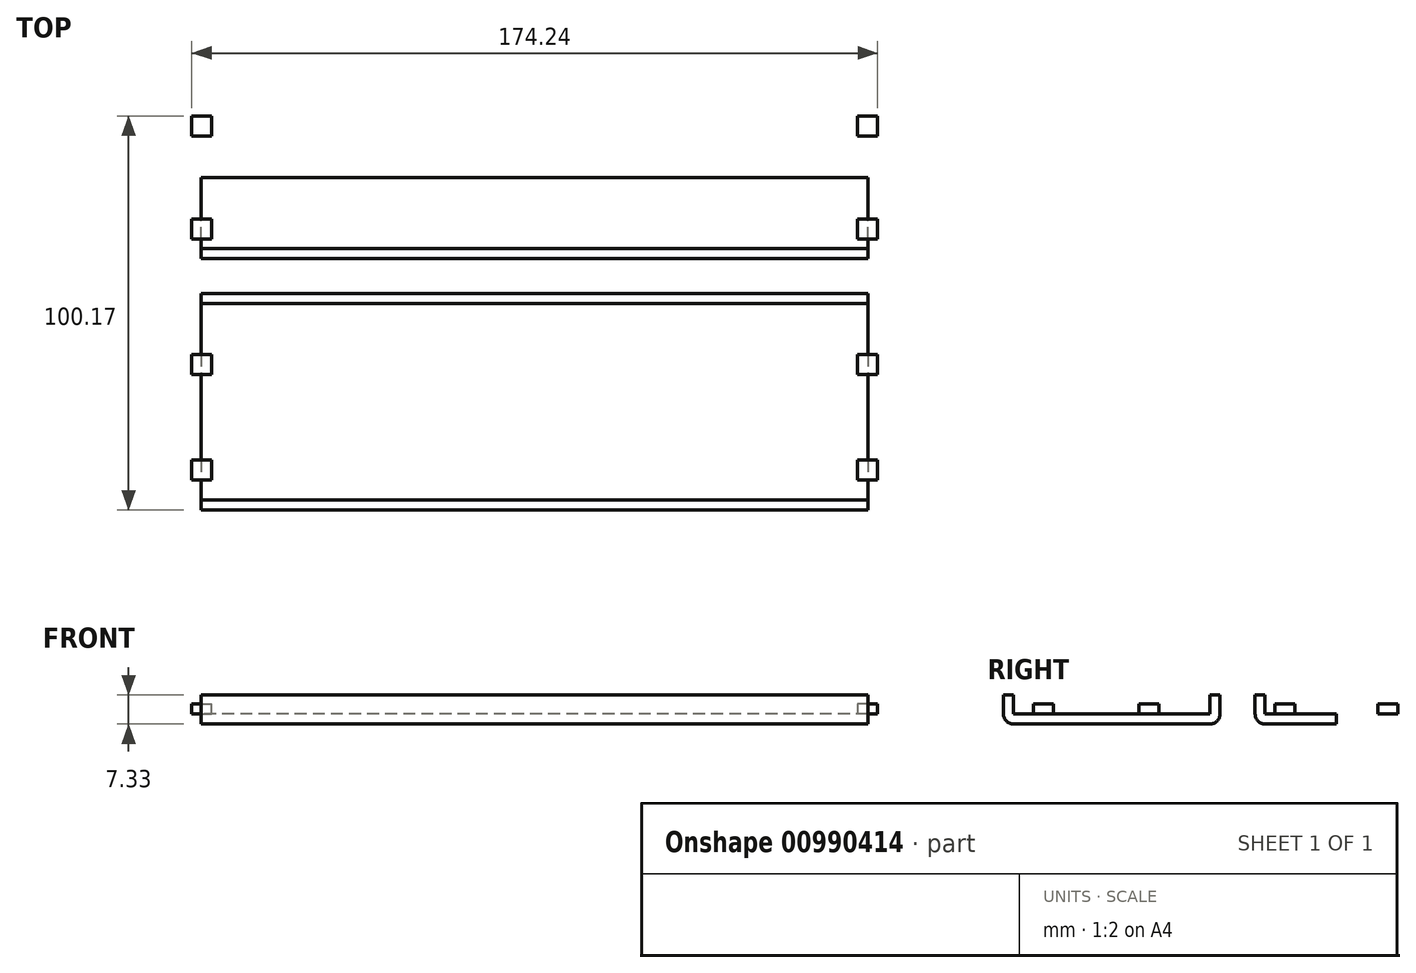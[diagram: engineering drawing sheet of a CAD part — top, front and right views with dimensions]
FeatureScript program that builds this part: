
annotation { "Feature Type Name" : "Feature", "Feature Type Description" : "" }
export const myFeature = defineFeature(function(context is Context, id is Id, definition is map)
    precondition{}
    {
        {
            var Q0;
            Q0=qCreatedBy(makeId("Right.planeOp"),FACE);
            var sketch = newSketch(context, id + "F0", { "sketchPlane" : qUnion([Q0])});
            skLineSegment(sketch, "E0", {"start": v(0, 0) * mm, "end": v(0, 169.34) * mm});
            skLineSegment(sketch, "E1", {"start": v(0, 169.34) * mm, "end": v(200.4, 169.34) * mm});
            skLineSegment(sketch, "E2", {"start": v(0, 0) * mm, "end": v(43.05, 0) * mm, "construction": true});
            skLineSegment(sketch, "E3", {"start": v(43.05, 0) * mm, "end": v(23.47, 45.96) * mm});
            skLineSegment(sketch, "E4", {"start": v(0, 47.82) * mm, "end": v(22.68, 47.82) * mm, "construction": true});
            skLineSegment(sketch, "E5", {"start": v(22.68, 47.82) * mm, "end": v(22.68, 0) * mm, "construction": true});
            skLineSegment(sketch, "E6", {"start": v(23.1, 49.8) * mm, "end": v(40.9, 132) * mm});
            skLineSegment(sketch, "E7", {"start": v(41.4, 134.33) * mm, "end": v(0, 134.33) * mm, "construction": true});
            skLineSegment(sketch, "E8", {"start": v(41.4, 134.33) * mm, "end": v(43.05, 0) * mm, "construction": true});
            skLineSegment(sketch, "E9", {"start": v(43.31, 135.75) * mm, "end": v(72.51, 157.5) * mm});
            skLineSegment(sketch, "E10", {"start": v(74.2, 158.76) * mm, "end": v(74.2, 169.34) * mm, "construction": true});
            skLineSegment(sketch, "E11", {"start": v(74.2, 158.76) * mm, "end": v(0, 158.76) * mm, "construction": true});
            skPoint(sketch, "E12", {"position": v(100.2, 169.34) * mm});
            skLineSegment(sketch, "E13", {"start": v(100.2, 169.34) * mm, "end": v(100.2, 154.3) * mm, "construction": true});
            skLineSegment(sketch, "E14", {"start": v(76.3, 158.76) * mm, "end": v(100.2, 158.76) * mm});
            skLineSegment(sketch, "E15.4", {"start": v(41.18, -0.8) * mm, "end": v(20.56, 47.62) * mm, "construction": true});
            skLineSegment(sketch, "E15.5", {"start": v(20.56, 47.62) * mm, "end": v(39.58, 135.5) * mm});
            skLineSegment(sketch, "E15.6", {"start": v(39.58, 135.5) * mm, "end": v(73.52, 160.79) * mm});
            skLineSegment(sketch, "E15.7", {"start": v(73.52, 160.79) * mm, "end": v(100.2, 160.79) * mm});
            skLineSegment(sketch, "E16.5", {"start": v(11.62, 46.77) * mm, "end": v(31.89, 140.45) * mm});
            skLineSegment(sketch, "E16.6", {"start": v(31.89, 140.45) * mm, "end": v(70.69, 169.35) * mm, "construction": true});
            skLineSegment(sketch, "E16.7", {"start": v(70.69, 169.35) * mm, "end": v(100.2, 169.35) * mm});
            skLineSegment(sketch, "E17", {"start": v(31.89, 140.45) * mm, "end": v(38.14, 169.34) * mm, "construction": true});
            skLineSegment(sketch, "E18", {"start": v(10.6, 158.76) * mm, "end": v(0, 158.76) * mm, "construction": true});
            skLineSegment(sketch, "E19", {"start": v(10.6, 158.76) * mm, "end": v(10.6, 46.77) * mm});
            skLineSegment(sketch, "E20", {"start": v(10.6, 46.77) * mm, "end": v(11.62, 46.77) * mm});
            skLineSegment(sketch, "E21", {"start": v(36.3, 160.79) * mm, "end": v(31.89, 140.45) * mm, "construction": true});
            skLineSegment(sketch, "E22", {"start": v(41.4, 134.33) * mm, "end": v(48.98, 169.34) * mm, "construction": true});
            skLineSegment(sketch, "E23", {"start": v(47.13, 160.79) * mm, "end": v(44.8, 150.07) * mm});
            skLineSegment(sketch, "E24", {"start": v(13.2, 0) * mm, "end": v(0, 0) * mm});
            skLineSegment(sketch, "E25", {"start": v(31.54, 0) * mm, "end": v(43.05, 0) * mm});
            skLineSegment(sketch, "E26", {"start": v(100.2, 158.76) * mm, "end": v(100.2, 169.35) * mm});
            skPoint(sketch, "E27", {"position": v(46.69, 158.76) * mm});
            skPoint(sketch, "E28", {"position": v(56.47, 158.76) * mm});
            skLineSegment(sketch, "E29", {"start": v(46.69, 158.76) * mm, "end": v(56.47, 158.76) * mm});
            skLineSegment(sketch, "E30", {"start": v(44.8, 150.07) * mm, "end": v(46.69, 158.76) * mm});
            skLineSegment(sketch, "E31", {"start": v(10.6, 158.76) * mm, "end": v(35.85, 158.76) * mm});
            skLineSegment(sketch, "E32", {"start": v(35.85, 158.76) * mm, "end": v(31.89, 140.45) * mm});
            skLineSegment(sketch, "E33", {"start": v(44.8, 150.07) * mm, "end": v(56.47, 158.76) * mm});
            skLineSegment(sketch, "E34", {"start": v(30.88, 85.7) * mm, "end": v(20.53, 87.94) * mm, "construction": true});
            skLineSegment(sketch, "E35.0", {"start": v(33.3, -4.15) * mm, "end": v(12.94, 43.67) * mm, "construction": true});
            skLineSegment(sketch, "E36", {"start": v(22.68, 47.82) * mm, "end": v(18.8, 29.9) * mm, "construction": true});
            skLineSegment(sketch, "E37", {"start": v(18.8, 29.9) * mm, "end": v(12.34, 0) * mm});
            skLineSegment(sketch, "E38", {"start": v(18.8, 29.9) * mm, "end": v(31.54, 0) * mm});
            skLineSegment(sketch, "E39", {"start": v(12.34, 0) * mm, "end": v(31.54, 0) * mm});
            skLineSegment(sketch, "E40", {"start": v(20.56, 47.62) * mm, "end": v(40.84, 0) * mm});
            skPoint(sketch, "E41.visualSharp", {"position": v(41.4, 134.33) * mm});
            skArc(sketch, "E41.filletArc", {"start": v(43.31, 135.75) * mm, "mid": v(41.77, 134.1) * mm, "end": v(40.9, 132) * mm});
            skPoint(sketch, "E42.visualSharp", {"position": v(22.68, 47.82) * mm});
            skArc(sketch, "E42.filletArc", {"start": v(23.1, 49.8) * mm, "mid": v(23, 47.85) * mm, "end": v(23.47, 45.96) * mm});
            skPoint(sketch, "E43.visualSharp", {"position": v(74.2, 158.76) * mm});
            skArc(sketch, "E43.filletArc", {"start": v(76.3, 158.76) * mm, "mid": v(74.3, 158.44) * mm, "end": v(72.51, 157.5) * mm});
            skPoint(sketch, "E44", {"position": v(21.75, 93.6) * mm});
            skLineSegment(sketch, "E45", {"start": v(21.75, 93.6) * mm, "end": v(22.1, 95.21) * mm});
            skLineSegment(sketch, "E46", {"start": v(22.1, 95.21) * mm, "end": v(26.54, 94.25) * mm});
            skLineSegment(sketch, "E47", {"start": v(29.56, 96.2) * mm, "end": v(37.5, 132.86) * mm});
            skLineSegment(sketch, "E48", {"start": v(35.55, 135.88) * mm, "end": v(31.1, 136.84) * mm});
            skPoint(sketch, "E49.visualSharp", {"position": v(38.03, 135.35) * mm});
            skArc(sketch, "E49.filletArc", {"start": v(37.5, 132.86) * mm, "mid": v(37.15, 134.78) * mm, "end": v(35.55, 135.88) * mm});
            skPoint(sketch, "E50.visualSharp", {"position": v(29.02, 93.72) * mm});
            skArc(sketch, "E50.filletArc", {"start": v(26.54, 94.25) * mm, "mid": v(28.45, 94.6) * mm, "end": v(29.56, 96.2) * mm});
            skLineSegment(sketch, "E51", {"start": v(21.75, 93.6) * mm, "end": v(32.1, 91.37) * mm, "construction": true});
            skLineSegment(sketch, "E52.0", {"start": v(35.01, 133.4) * mm, "end": v(30.57, 134.36) * mm});
            skLineSegment(sketch, "E52.1", {"start": v(22.64, 97.7) * mm, "end": v(27.08, 96.74) * mm});
            skLineSegment(sketch, "E52.2", {"start": v(27.08, 96.74) * mm, "end": v(27.08, 96.74) * mm});
            skLineSegment(sketch, "E52.3", {"start": v(27.08, 96.74) * mm, "end": v(35.01, 133.4) * mm});
            skLineSegment(sketch, "E52.4", {"start": v(35.01, 133.4) * mm, "end": v(35.01, 133.4) * mm});
            skLineSegment(sketch, "E53.MirrorCS", {"start": v(21.4, 92) * mm, "end": v(25.85, 91.04) * mm});
            skArc(sketch, "E54.MirrorCS", {"start": v(25.85, 91.04) * mm, "mid": v(27.44, 89.94) * mm, "end": v(27.8, 88.02) * mm});
            skLineSegment(sketch, "E55.MirrorCS", {"start": v(27.8, 88.02) * mm, "end": v(19.86, 51.36) * mm});
            skArc(sketch, "E56.MirrorCS", {"start": v(19.86, 51.36) * mm, "mid": v(18.75, 49.76) * mm, "end": v(16.84, 49.41) * mm});
            skLineSegment(sketch, "E57.MirrorCS", {"start": v(16.84, 49.41) * mm, "end": v(12.4, 50.38) * mm});
            skLineSegment(sketch, "E58.MirrorCS", {"start": v(17.37, 51.9) * mm, "end": v(12.94, 52.86) * mm});
            skLineSegment(sketch, "E59.MirrorCS", {"start": v(25.3, 88.56) * mm, "end": v(17.37, 51.9) * mm});
            skLineSegment(sketch, "E60.MirrorCS", {"start": v(20.87, 89.52) * mm, "end": v(25.3, 88.56) * mm});
            skLineSegment(sketch, "E61", {"start": v(33.72, 127.42) * mm, "end": v(31.23, 127.96) * mm});
            skLineSegment(sketch, "E62", {"start": v(31.23, 127.96) * mm, "end": v(30.16, 123) * mm});
            skLineSegment(sketch, "E63", {"start": v(30.16, 123) * mm, "end": v(32.64, 122.46) * mm});
            skLineSegment(sketch, "E64", {"start": v(28.37, 102.7) * mm, "end": v(25.88, 103.24) * mm});
            skLineSegment(sketch, "E65", {"start": v(25.88, 103.24) * mm, "end": v(26.96, 108.2) * mm});
            skLineSegment(sketch, "E66", {"start": v(26.96, 108.2) * mm, "end": v(29.44, 107.66) * mm});
            skLineSegment(sketch, "E67.MirrorCS", {"start": v(24.02, 82.6) * mm, "end": v(21.54, 83.13) * mm});
            skLineSegment(sketch, "E68.MirrorCS", {"start": v(21.54, 83.13) * mm, "end": v(20.46, 78.17) * mm});
            skLineSegment(sketch, "E69.MirrorCS", {"start": v(20.46, 78.17) * mm, "end": v(22.94, 77.63) * mm});
            skLineSegment(sketch, "E70.MirrorCS", {"start": v(17.26, 63.37) * mm, "end": v(19.74, 62.84) * mm});
            skLineSegment(sketch, "E71.MirrorCS", {"start": v(16.19, 58.4) * mm, "end": v(17.26, 63.37) * mm});
            skLineSegment(sketch, "E72.MirrorCS", {"start": v(18.67, 57.87) * mm, "end": v(16.19, 58.4) * mm});
            skLineSegment(sketch, "E73", {"start": v(31.89, 140.45) * mm, "end": v(41.4, 134.33) * mm, "construction": true});
            skLineSegment(sketch, "E74.MirrorCS", {"start": v(37.56, 139.02) * mm, "end": v(34.85, 142.66) * mm});
            skArc(sketch, "E75.MirrorCS", {"start": v(41.12, 138.5) * mm, "mid": v(39.23, 138.02) * mm, "end": v(37.56, 139.02) * mm});
            skLineSegment(sketch, "E76.MirrorCS", {"start": v(71.2, 160.9) * mm, "end": v(41.12, 138.5) * mm});
            skArc(sketch, "E77.MirrorCS", {"start": v(71.72, 164.46) * mm, "mid": v(72.2, 162.57) * mm, "end": v(71.2, 160.9) * mm});
            skLineSegment(sketch, "E78.MirrorCS", {"start": v(69, 168.1) * mm, "end": v(71.72, 164.46) * mm});
            skLineSegment(sketch, "E79.MirrorCS", {"start": v(66.97, 166.58) * mm, "end": v(69.69, 162.94) * mm});
            skLineSegment(sketch, "E80.MirrorCS", {"start": v(69.69, 162.94) * mm, "end": v(39.6, 140.53) * mm});
            skLineSegment(sketch, "E81.MirrorCS", {"start": v(64.8, 159.3) * mm, "end": v(63.28, 161.33) * mm});
            skLineSegment(sketch, "E82.MirrorCS", {"start": v(63.28, 161.33) * mm, "end": v(59.2, 158.3) * mm});
            skLineSegment(sketch, "E83.MirrorCS", {"start": v(59.2, 158.3) * mm, "end": v(60.72, 156.26) * mm});
            skLineSegment(sketch, "E84.MirrorCS", {"start": v(47.06, 149.26) * mm, "end": v(48.58, 147.22) * mm});
            skLineSegment(sketch, "E85.MirrorCS", {"start": v(42.99, 146.22) * mm, "end": v(47.06, 149.26) * mm});
            skLineSegment(sketch, "E86.MirrorCS", {"start": v(44.5, 144.19) * mm, "end": v(42.99, 146.22) * mm});
            skLineSegment(sketch, "E87.MirrorCS", {"start": v(39.6, 140.53) * mm, "end": v(36.89, 144.18) * mm});
            skLineSegment(sketch, "E88", {"start": v(70.69, 169.35) * mm, "end": v(70.69, 164.55) * mm});
            skPoint(sketch, "E89.visualSharp", {"position": v(70.69, 162) * mm});
            skArc(sketch, "E89.filletArc", {"start": v(68.15, 162) * mm, "mid": v(69.94, 162.75) * mm, "end": v(70.69, 164.55) * mm});
            skLineSegment(sketch, "E90.1", {"start": v(68.15, 169.63) * mm, "end": v(68.15, 164.55) * mm});
            skLineSegment(sketch, "E91", {"start": v(55.17, 164.55) * mm, "end": v(55.17, 167.09) * mm});
            skLineSegment(sketch, "E92", {"start": v(55.17, 167.09) * mm, "end": v(50.1, 167.09) * mm});
            skLineSegment(sketch, "E93", {"start": v(50.1, 167.09) * mm, "end": v(50.1, 164.55) * mm});
            skLineSegment(sketch, "E94", {"start": v(28.37, 164.55) * mm, "end": v(28.37, 167.09) * mm});
            skLineSegment(sketch, "E95", {"start": v(28.37, 167.09) * mm, "end": v(23.3, 167.09) * mm});
            skLineSegment(sketch, "E96", {"start": v(23.3, 167.09) * mm, "end": v(23.3, 164.55) * mm});
            skLineSegment(sketch, "E97", {"start": v(22.68, 47.82) * mm, "end": v(11.62, 46.77) * mm, "construction": true});
            skLineSegment(sketch, "E98", {"start": v(15.36, 37.97) * mm, "end": v(19.78, 39.85) * mm});
            skLineSegment(sketch, "E99", {"start": v(23.11, 38.51) * mm, "end": v(37.3, 5.2) * mm});
            skLineSegment(sketch, "E100", {"start": v(35.96, 1.87) * mm, "end": v(31.54, -0.01) * mm});
            skPoint(sketch, "E101.visualSharp", {"position": v(38.3, 2.87) * mm});
            skArc(sketch, "E101.filletArc", {"start": v(35.96, 1.87) * mm, "mid": v(37.32, 3.26) * mm, "end": v(37.3, 5.2) * mm});
            skPoint(sketch, "E102.visualSharp", {"position": v(22.12, 40.85) * mm});
            skArc(sketch, "E102.filletArc", {"start": v(23.11, 38.51) * mm, "mid": v(21.72, 39.87) * mm, "end": v(19.78, 39.85) * mm});
            skLineSegment(sketch, "E103.0", {"start": v(34.97, 4.2) * mm, "end": v(25.52, 0.18) * mm});
            skLineSegment(sketch, "E103.1", {"start": v(20.78, 37.52) * mm, "end": v(34.97, 4.2) * mm});
            skLineSegment(sketch, "E103.2", {"start": v(16.36, 35.63) * mm, "end": v(20.78, 37.52) * mm});
            skLineSegment(sketch, "E104", {"start": v(27.86, 20.9) * mm, "end": v(25.52, 19.9) * mm});
            skLineSegment(sketch, "E105", {"start": v(25.52, 19.9) * mm, "end": v(23.53, 24.57) * mm});
            skLineSegment(sketch, "E106", {"start": v(23.53, 24.57) * mm, "end": v(25.87, 25.57) * mm});
            skLineSegment(sketch, "E107", {"start": v(21.48, 35.85) * mm, "end": v(19.15, 34.86) * mm});
            skLineSegment(sketch, "E108", {"start": v(19.15, 34.86) * mm, "end": v(21.14, 30.18) * mm});
            skLineSegment(sketch, "E109", {"start": v(21.14, 30.18) * mm, "end": v(23.48, 31.18) * mm});
            skLineSegment(sketch, "E110", {"start": v(79.6, 169.35) * mm, "end": v(79.6, 164.55) * mm});
            skLineSegment(sketch, "E111", {"start": v(82.14, 162) * mm, "end": v(100.2, 162) * mm});
            skPoint(sketch, "E112.visualSharp", {"position": v(79.6, 162) * mm});
            skArc(sketch, "E112.filletArc", {"start": v(79.6, 164.55) * mm, "mid": v(80.34, 162.75) * mm, "end": v(82.14, 162) * mm});
            skLineSegment(sketch, "E113.0", {"start": v(82.14, 164.55) * mm, "end": v(100.2, 164.55) * mm});
            skLineSegment(sketch, "E113.1", {"start": v(82.14, 169.35) * mm, "end": v(82.14, 164.55) * mm});
            skLineSegment(sketch, "E114", {"start": v(84.57, 164.55) * mm, "end": v(84.57, 167.09) * mm});
            skPoint(sketch, "E114.endSnap0", {"position": v(68.15, 167.09) * mm});
            skLineSegment(sketch, "E115", {"start": v(84.57, 167.09) * mm, "end": v(89.65, 167.09) * mm});
            skLineSegment(sketch, "E116", {"start": v(89.65, 167.09) * mm, "end": v(89.65, 164.55) * mm});
            skLineSegment(sketch, "E117", {"start": v(10.6, 158.76) * mm, "end": v(10.6, 164.55) * mm, "construction": true});
            skLineSegment(sketch, "E118", {"start": v(68.15, 164.55) * mm, "end": v(18.21, 164.55) * mm});
            skLineSegment(sketch, "E119", {"start": v(68.15, 162) * mm, "end": v(18.21, 162) * mm});
            skLineSegment(sketch, "E120", {"start": v(18.21, 164.55) * mm, "end": v(18.21, 169.34) * mm});
            skLineSegment(sketch, "E121", {"start": v(15.67, 164.55) * mm, "end": v(15.67, 169.34) * mm});
            skPoint(sketch, "E122.visualSharp", {"position": v(15.67, 162) * mm});
            skArc(sketch, "E122.filletArc", {"start": v(15.67, 164.55) * mm, "mid": v(16.42, 162.75) * mm, "end": v(18.21, 162) * mm});
            skLineSegment(sketch, "E123", {"start": v(15.67, 164.55) * mm, "end": v(18.21, 164.55) * mm, "construction": true});
            skLineSegment(sketch, "E124", {"start": v(10.6, 164.55) * mm, "end": v(15.67, 164.55) * mm, "construction": true});
            skLineSegment(sketch, "E125", {"start": v(23.3, 165.82) * mm, "end": v(18.21, 165.82) * mm, "construction": true});
            skLineSegment(sketch, "E126.MirrorCS", {"start": v(118.27, 164.55) * mm, "end": v(100.2, 164.55) * mm});
            skLineSegment(sketch, "E127.MirrorCS", {"start": v(110.76, 167.09) * mm, "end": v(110.76, 164.55) * mm});
            skLineSegment(sketch, "E128.MirrorCS", {"start": v(115.84, 167.09) * mm, "end": v(110.76, 167.09) * mm});
            skLineSegment(sketch, "E129.MirrorCS", {"start": v(115.84, 164.55) * mm, "end": v(115.84, 167.09) * mm});
            skLineSegment(sketch, "E130.MirrorCS", {"start": v(118.27, 169.35) * mm, "end": v(118.27, 164.55) * mm});
            skLineSegment(sketch, "E131.MirrorCS", {"start": v(120.8, 169.35) * mm, "end": v(120.8, 164.55) * mm});
            skArc(sketch, "E132.MirrorCS", {"start": v(120.8, 164.55) * mm, "mid": v(120.06, 162.75) * mm, "end": v(118.27, 162) * mm});
            skLineSegment(sketch, "E133.MirrorCS", {"start": v(118.27, 162) * mm, "end": v(100.2, 162) * mm});
            skSolve(sketch);
        }
        {
            var Q0;
            {var subQ16=sQuery(id+"F0.wireOp",EDGE,"E119");Q0=makeQuery(id+"F0.imprint","IMPRINT",FACE,{"disambiguationData":[TD([[makeQuery(id+"F0.imprint","IMPRINT",EDGE,{"derivedFrom":subQ16}),-1.0]])]});}
            var Q1;
            {var subQ0=sQuery(id+"F0.wireOp",EDGE,"E88");var subQ1=makeQuery(id+"F0.imprint","IMPRINT",VERTEX,{"derivedFrom":subQ0});Q1=makeQuery(id+"F0.imprint","IMPRINT",FACE,{"disambiguationData":[TD([[makeQuery(id+"F0.imprint","IMPRINT",EDGE,{"disambiguationData":[TD([[subQ1,1.0]])],"derivedFrom":subQ0}),-1.0]])]});}
            var Q2;
            {var subQ0=sQuery(id+"F0.wireOp",EDGE,"E111");Q2=makeQuery(id+"F0.imprint","IMPRINT",FACE,{"disambiguationData":[TD([[makeQuery(id+"F0.imprint","IMPRINT",EDGE,{"derivedFrom":subQ0}),1.0]])]});}
            var Q3;
            {var subQ12=sQuery(id+"F0.wireOp",EDGE,"E132.MirrorCS");Q3=makeQuery(id+"F0.imprint","IMPRINT",FACE,{"disambiguationData":[TD([[makeQuery(id+"F0.imprint","IMPRINT",EDGE,{"derivedFrom":subQ12}),-1.0]])]});}
            extrude(context, id + "F1", {"entities" : qUnion([Q0, Q1, Q2, Q3]), "endBound" : BoundingType.SYMMETRIC, "depth" : 169.34 * mm, "offsetDistance" : 25.4 * mm});
        }
        {
            var Q0;
            {var subQ0=sQuery(id+"F0.wireOp",EDGE,"E91");Q0=makeQuery(id+"F0.imprint","IMPRINT",FACE,{"disambiguationData":[TD([[makeQuery(id+"F0.imprint","IMPRINT",EDGE,{"derivedFrom":subQ0}),1.0]])]});}
            var Q1;
            {var subQ0=sQuery(id+"F0.wireOp",EDGE,"E94");Q1=makeQuery(id+"F0.imprint","IMPRINT",FACE,{"disambiguationData":[TD([[makeQuery(id+"F0.imprint","IMPRINT",EDGE,{"derivedFrom":subQ0}),1.0]])]});}
            var Q2;
            {var subQ0=sQuery(id+"F0.wireOp",EDGE,"E114");Q2=makeQuery(id+"F0.imprint","IMPRINT",FACE,{"disambiguationData":[TD([[makeQuery(id+"F0.imprint","IMPRINT",EDGE,{"derivedFrom":subQ0}),-1.0]])]});}
            var Q3;
            {var subQ0=sQuery(id+"F0.wireOp",EDGE,"E127.MirrorCS");Q3=makeQuery(id+"F0.imprint","IMPRINT",FACE,{"disambiguationData":[TD([[makeQuery(id+"F0.imprint","IMPRINT",EDGE,{"derivedFrom":subQ0}),1.0]])]});}
            extrude(context, id + "F2", {"entities" : qUnion([Q0, Q1, Q2, Q3]), "operationType" : NewBodyOperationType.ADD, "depth" : 87.12 * mm, "offsetDistance" : 25.4 * mm, "hasSecondDirection" : true, "secondDirectionOppositeDirection" : true, "secondDirectionDepth" : -82.04 * mm});
        }
        {
            var Q0;
            {var subQ0=sQuery(id+"F0.wireOp",EDGE,"E94");Q0=makeQuery(id+"F0.imprint","IMPRINT",FACE,{"disambiguationData":[TD([[makeQuery(id+"F0.imprint","IMPRINT",EDGE,{"derivedFrom":subQ0}),1.0]])]});}
            var Q1;
            {var subQ0=sQuery(id+"F0.wireOp",EDGE,"E91");Q1=makeQuery(id+"F0.imprint","IMPRINT",FACE,{"disambiguationData":[TD([[makeQuery(id+"F0.imprint","IMPRINT",EDGE,{"derivedFrom":subQ0}),1.0]])]});}
            var Q2;
            {var subQ0=sQuery(id+"F0.wireOp",EDGE,"E114");Q2=makeQuery(id+"F0.imprint","IMPRINT",FACE,{"disambiguationData":[TD([[makeQuery(id+"F0.imprint","IMPRINT",EDGE,{"derivedFrom":subQ0}),-1.0]])]});}
            var Q3;
            {var subQ0=sQuery(id+"F0.wireOp",EDGE,"E127.MirrorCS");Q3=makeQuery(id+"F0.imprint","IMPRINT",FACE,{"disambiguationData":[TD([[makeQuery(id+"F0.imprint","IMPRINT",EDGE,{"derivedFrom":subQ0}),1.0]])]});}
            extrude(context, id + "F3", {"entities" : qUnion([Q0, Q1, Q2, Q3]), "operationType" : NewBodyOperationType.ADD, "depth" : -87.12 * mm, "offsetDistance" : 25.4 * mm, "hasSecondDirection" : true, "secondDirectionOppositeDirection" : true, "secondDirectionDepth" : 82.04 * mm});
        }
    });
